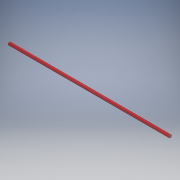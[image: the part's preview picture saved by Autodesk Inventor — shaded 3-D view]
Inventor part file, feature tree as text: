
AUTODESK INVENTOR PART (.ipt)
format: ipt  version: 2017 SP1 (Build 210196100, 196)  size: 109,056 bytes
history: native  units: mm
features: extrude x1, sketch x1
ambient origin geometry x8: Origin, YZ Plane, XZ Plane, XY Plane, X Axis, Y Axis, Z Axis, Center Point
bodies: Solid1 (feature_tree)
feature tree (2):
  extrude  "Extrusion1"  Depth=165.0mm TaperAngle=0.0deg
  sketch  "Sketch2"  dims[d0=3.0mm d1=165.0mm d2=0.0mm]
